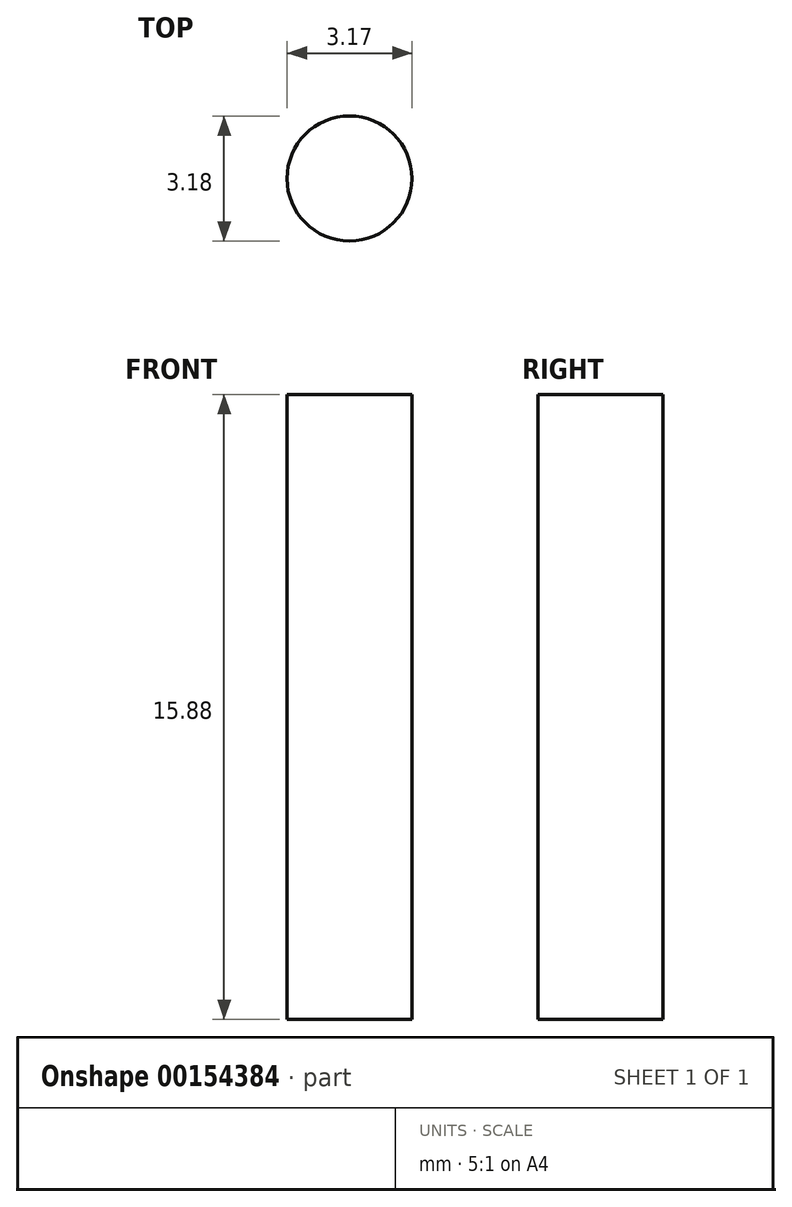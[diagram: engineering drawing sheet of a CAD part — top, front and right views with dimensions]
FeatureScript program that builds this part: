
annotation { "Feature Type Name" : "Feature", "Feature Type Description" : "" }
export const myFeature = defineFeature(function(context is Context, id is Id, definition is map)
    precondition{}
    {
        {
            var Q0;
            Q0=qCreatedBy(makeId("Top.planeOp"),FACE);
            var sketch = newSketch(context, id + "F0", { "sketchPlane" : qUnion([Q0])});
            skCircle(sketch, "E0", {"center": v(45.05, 50.8) * mm, "radius": 1.59 * mm});
            skSolve(sketch);
        }
        {
            var Q0;
            Q0=makeQuery(id+"F0.imprint","IMPRINT",FACE,{"disambiguationData":[TD([[makeQuery(id+"F0.imprint","IMPRINT",EDGE,{"derivedFrom":sQuery(id+"F0.wireOp",EDGE,"E0")}),1.0]])]});
            extrude(context, id + "F1", {"entities" : qUnion([Q0]), "depth" : 15.88 * mm});
        }
    });
